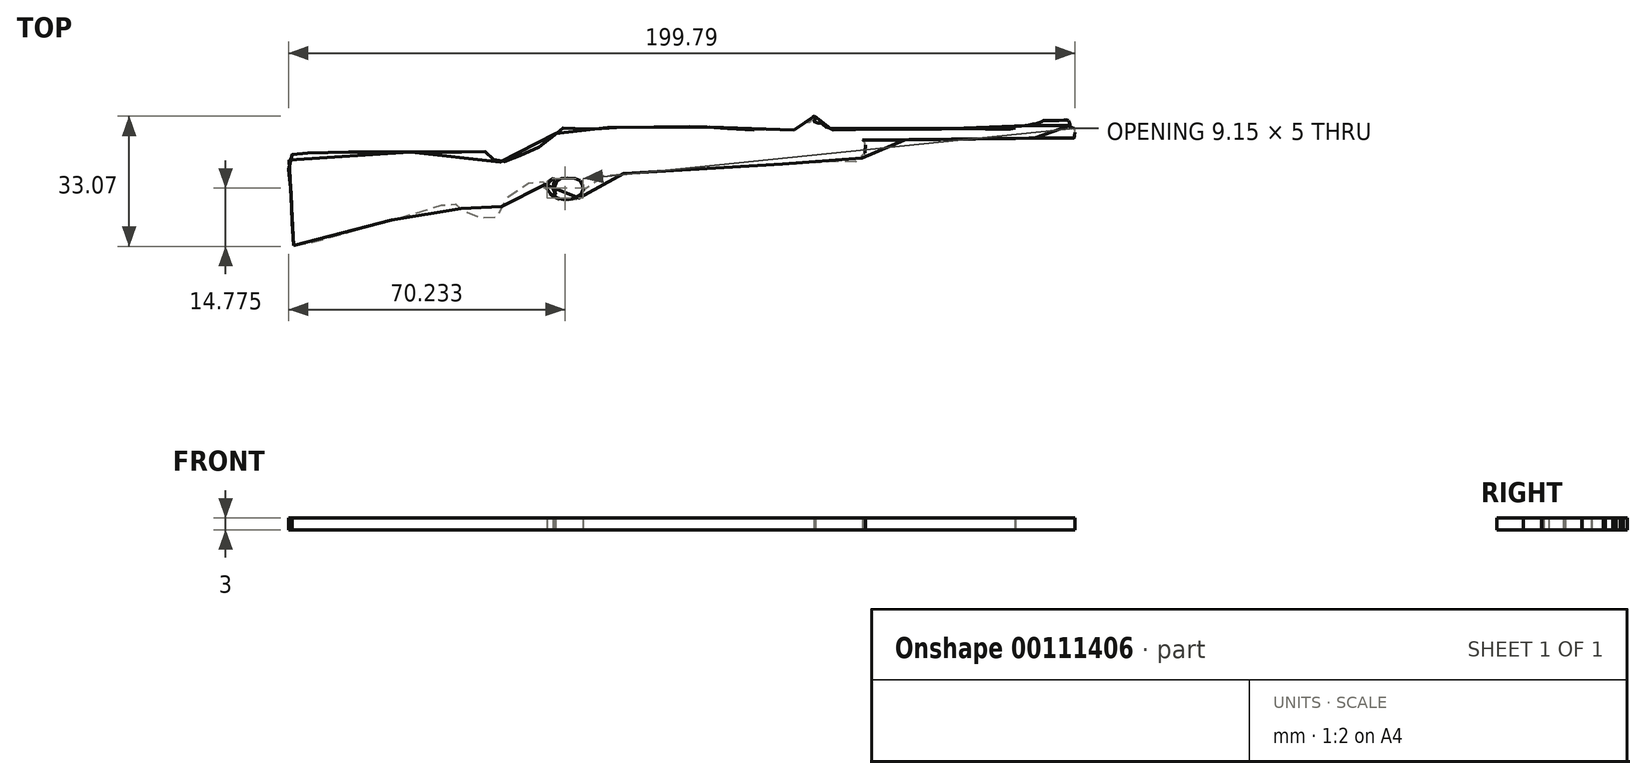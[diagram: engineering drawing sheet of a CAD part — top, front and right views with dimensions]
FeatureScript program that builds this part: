
annotation { "Feature Type Name" : "Feature", "Feature Type Description" : "" }
export const myFeature = defineFeature(function(context is Context, id is Id, definition is map)
    precondition{}
    {
        {
            var Q0;
            Q0=qCreatedBy(makeId("Top.planeOp"),FACE);
            var sketch = newSketch(context, id + "F0", { "sketchPlane" : qUnion([Q0])});
            skFitSpline(sketch, "E0", {"points": [v(-83.3, -6.7) * mm, v(-82.47, -6.85) * mm, v(-77.99, -5.7) * mm, v(-67.53, -2.8) * mm, v(-47.34, 3.04) * mm, v(-44.33, 3.98) * mm, v(-42.88, 4.03) * mm, v(-41.72, 3.7) * mm, v(-41, 3.1) * mm, v(-40.74, 2.5) * mm, v(-40.48, 2.27) * mm, v(-39.17, 1.56) * mm, v(-35.84, 0.4) * mm, v(-31.92, -0.15) * mm, v(-31.84, -0.09) * mm, v(-30.72, 2.92) * mm, v(-28.92, 5.68) * mm, v(-25.15, 8.53) * mm, v(-20.76, 9.97) * mm, v(-20.37, 9.97) * mm, v(-19.92, 9.54) * mm, v(-19.38, 8.8) * mm, v(-19.28, 8) * mm, v(-18.98, 6.48) * mm, v(-17.93, 5.51) * mm, v(-15.3, 4.61) * mm, v(-13.06, 4.61) * mm, v(-11.19, 5.14) * mm, v(-9.92, 6.36) * mm, v(-9.17, 7.68) * mm, v(-7.8, 9.02) * mm, v(-4.28, 11.18) * mm, v(-3.53, 11.3) * mm, v(2.64, 11.7) * mm, v(8, 11.99) * mm, v(47.54, 14.34) * mm, v(56.35, 14.85) * mm, v(58.3, 14.93) * mm, v(59.84, 14.64) * mm, v(60.72, 15.06) * mm, v(61.6, 16.32) * mm, v(61.88, 18.1) * mm, v(61.64, 19.66) * mm, v(61.2, 20.07) * mm, v(63.12, 20.13) * mm, v(73.33, 20.17) * mm, v(86.25, 20.33) * mm, v(105.7, 20.58) * mm, v(114.83, 20.63) * mm, v(114.94, 20.66) * mm, v(115.09, 21.3) * mm, v(115.17, 22.33) * mm, v(114.85, 23.2) * mm, v(114.4, 23.2) * mm, v(114.1, 23.2) * mm, v(113.79, 24.18) * mm, v(113.44, 25.1) * mm, v(112.2, 25.17) * mm, v(107.37, 25.1) * mm, v(107.17, 25.08) * mm, v(106.65, 24.73) * mm, v(104.48, 24.15) * mm, v(101.39, 23.66) * mm, v(99.97, 23.55) * mm, v(99.97, 23.35) * mm, v(99.92, 23.14) * mm, v(93.8, 22.94) * mm, v(78.8, 22.94) * mm, v(54.38, 22.72) * mm, v(53.36, 22.72) * mm, v(53.33, 22.82) * mm, v(53.23, 23.02) * mm, v(52.88, 23.1) * mm, v(52.19, 23.3) * mm, v(51.22, 23.88) * mm, v(50.8, 24.33) * mm, v(50.33, 24.5) * mm, v(49.8, 24.48) * mm, v(49.77, 24.6) * mm, v(49.54, 24.6) * mm, v(48.9, 24.65) * mm, v(49.02, 25.05) * mm, v(49.24, 25.93) * mm, v(49.04, 26.15) * mm, v(48.67, 26.14) * mm, v(48.48, 25.85) * mm, v(47.91, 24.61) * mm, v(47.76, 24.6) * mm, v(46.74, 24.5) * mm, v(46.53, 24.28) * mm, v(45.76, 23.64) * mm, v(44.58, 23.1) * mm, v(44.2, 22.98) * mm, v(44.09, 22.84) * mm, v(44.04, 22.64) * mm, v(43.45, 22.6) * mm, v(36.75, 22.64) * mm, v(28.25, 22.9) * mm, v(22.26, 23.41) * mm, v(20.26, 23.54) * mm, v(10.34, 23.41) * mm, v(-3.7, 23.22) * mm, v(-4.92, 23.15) * mm, v(-5.7, 22.9) * mm, v(-9.1, 22.96) * mm, v(-15.2, 23.13) * mm, v(-15.55, 22.82) * mm, v(-17.15, 21.39) * mm, v(-20.66, 18.47) * mm, v(-25.19, 16.37) * mm, v(-29.05, 14.83) * mm, v(-30.37, 14.5) * mm, v(-31.92, 14.83) * mm, v(-33.35, 15.82) * mm, v(-34.46, 17.03) * mm, v(-36.66, 17.14) * mm, v(-68.78, 17.03) * mm, v(-82.68, 16.7) * mm, v(-83.79, 16.37) * mm, v(-84.56, 14.39) * mm, v(-84.23, 9.42) * mm, v(-83.68, 0) * mm, v(-83.3, -6.7) * mm]});
            skFitSpline(sketch, "E1", {"points": [v(-18.95, 8.67) * mm, v(-18.53, 9.47) * mm, v(-17.93, 9.97) * mm, v(-17.26, 10.32) * mm, v(-16.82, 10.32) * mm, v(-16.8, 10.17) * mm, v(-17.15, 9.55) * mm, v(-17.31, 8.83) * mm, v(-17.38, 8.34) * mm, v(-17.25, 7.21) * mm, v(-16.79, 6.25) * mm, v(-16.79, 6.46) * mm, v(-16.82, 6.72) * mm, v(-17.1, 7.66) * mm, v(-16.97, 8.7) * mm, v(-16.38, 9.73) * mm, v(-15.4, 10.34) * mm, v(-14, 10.44) * mm, v(-12, 10.34) * mm, v(-11.06, 10.19) * mm, v(-10.2, 9.28) * mm, v(-9.85, 8.53) * mm, v(-9.78, 7.87) * mm, v(-9.92, 7.04) * mm, v(-10.5, 6.12) * mm, v(-11.57, 5.51) * mm, v(-12.6, 5.14) * mm, v(-14.32, 5) * mm, v(-15.84, 5.24) * mm, v(-17.56, 5.92) * mm, v(-18.6, 6.88) * mm, v(-18.99, 8) * mm, v(-18.95, 8.67) * mm]});
            skSolve(sketch);
        }
        {
            var Q0;
            Q0 = qSketchRegion(id + "F0", true);
            extrude(context, id + "F1", {"entities" : qUnion([Q0]), "depth" : 3 * mm});
        }
    });
